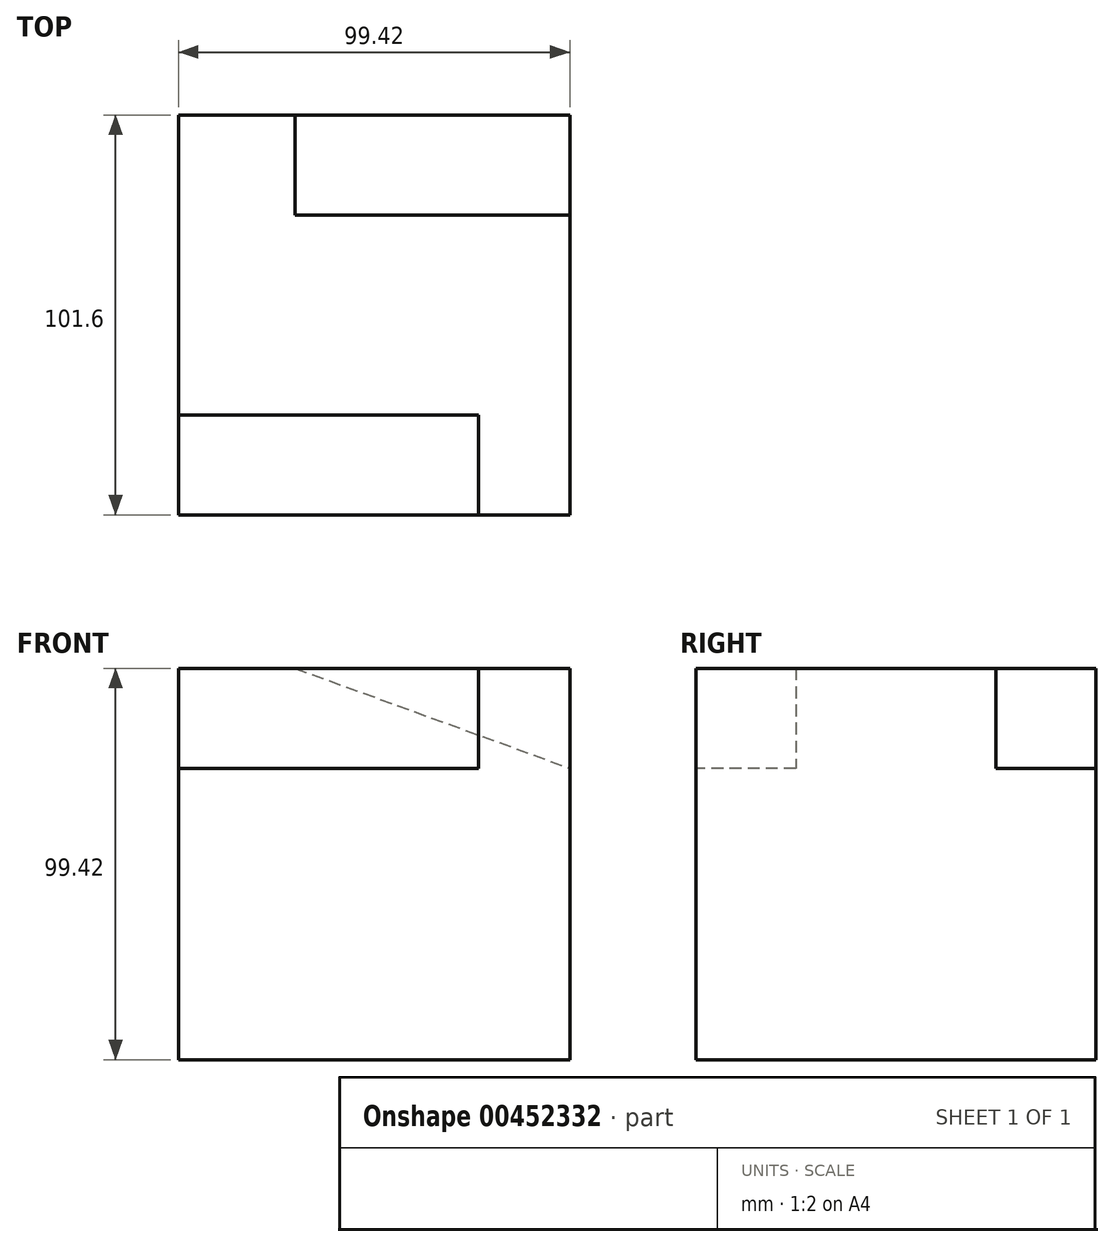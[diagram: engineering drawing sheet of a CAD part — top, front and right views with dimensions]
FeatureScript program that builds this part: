
annotation { "Feature Type Name" : "Feature", "Feature Type Description" : "" }
export const myFeature = defineFeature(function(context is Context, id is Id, definition is map)
    precondition{}
    {
        {
            var Q0;
            Q0=qCreatedBy(makeId("Front.planeOp"),FACE);
            var sketch = newSketch(context, id + "F0", { "sketchPlane" : qUnion([Q0])});
            skLineSegment(sketch, "E0.bottom", {"start": v(-49.71, 49.71) * mm, "end": v(49.71, 49.71) * mm});
            skLineSegment(sketch, "E0.top", {"start": v(-49.71, -49.71) * mm, "end": v(49.71, -49.71) * mm});
            skLineSegment(sketch, "E0.left", {"start": v(-49.71, 49.71) * mm, "end": v(-49.71, -49.71) * mm});
            skLineSegment(sketch, "E0.right", {"start": v(49.71, 49.71) * mm, "end": v(49.71, -49.71) * mm});
            skSolve(sketch);
        }
        {
            var Q0;
            Q0=makeQuery(id+"F0.imprint","IMPRINT",FACE,{"disambiguationData":[TD([[makeQuery(id+"F0.imprint","IMPRINT",EDGE,{"derivedFrom":sQuery(id+"F0.wireOp",EDGE,"E0.bottom")}),-1.0]])]});
            extrude(context, id + "F1", {"entities" : qUnion([Q0]), "endBound" : BoundingType.SYMMETRIC, "depth" : 101.6 * mm});
        }
        {
            var Q0;
            Q0=makeQuery(id+"F1.opExtrude","CAP_FACE",FACE,{"disambiguationData":[OSD([sQuery(id+"F0.wireOp",EDGE,"E0.bottom"),sQuery(id+"F0.wireOp",EDGE,"E0.top"),sQuery(id+"F0.wireOp",EDGE,"E0.left"),sQuery(id+"F0.wireOp",EDGE,"E0.right")])],"isStart":false});
            var sketch = newSketch(context, id + "F2", { "sketchPlane" : qUnion([Q0])});
            skLineSegment(sketch, "E1.bottom", {"start": v(-49.71, 49.71) * mm, "end": v(26.49, 49.71) * mm});
            skLineSegment(sketch, "E1.top", {"start": v(-49.71, 24.31) * mm, "end": v(26.49, 24.31) * mm});
            skLineSegment(sketch, "E1.left", {"start": v(-49.71, 49.71) * mm, "end": v(-49.71, 24.31) * mm});
            skLineSegment(sketch, "E1.right", {"start": v(26.49, 49.71) * mm, "end": v(26.49, 24.31) * mm});
            skSolve(sketch);
        }
        {
            var Q0;
            Q0=makeQuery(id+"F2.imprint","IMPRINT",FACE,{"disambiguationData":[TD([[makeQuery(id+"F2.imprint","IMPRINT",EDGE,{"derivedFrom":sQuery(id+"F2.wireOp",EDGE,"E1.bottom")}),-1.0]])]});
            extrude(context, id + "F3", {"entities" : qUnion([Q0]), "operationType" : NewBodyOperationType.REMOVE, "oppositeDirection" : true, "depth" : 25.4 * mm});
        }
        {
            var Q0;
            Q0=makeQuery(id+"F1.opExtrude","CAP_FACE",FACE,{"disambiguationData":[OSD([sQuery(id+"F0.wireOp",EDGE,"E0.bottom"),sQuery(id+"F0.wireOp",EDGE,"E0.top"),sQuery(id+"F0.wireOp",EDGE,"E0.left"),sQuery(id+"F0.wireOp",EDGE,"E0.right")])],"isStart":true});
            var sketch = newSketch(context, id + "F4", { "sketchPlane" : qUnion([Q0])});
            skLineSegment(sketch, "E2", {"start": v(20.07, 49.71) * mm, "end": v(-49.71, 24.31) * mm});
            skLineSegment(sketch, "E3", {"start": v(-49.71, 24.31) * mm, "end": v(-49.71, 49.71) * mm});
            skLineSegment(sketch, "E4", {"start": v(-49.71, 49.71) * mm, "end": v(20.07, 49.71) * mm});
            skSolve(sketch);
        }
        {
            var Q0;
            Q0 = qSketchRegion(id + "F4", true);
            extrude(context, id + "F5", {"entities" : qUnion([Q0]), "operationType" : NewBodyOperationType.REMOVE, "oppositeDirection" : true, "depth" : 25.4 * mm});
        }
        {
            var Q0;
            Q0=makeQuery(id+"F1.opExtrude","CAP_VERTEX",VERTEX,{"disambiguationData":[OSD([sQuery(id+"F0.wireOp",EDGE,"E0.bottom"),sQuery(id+"F0.wireOp",EDGE,"E0.right")])],"isStart":false});
            var Q1;
            Q1=makeQuery(id+"F1.opExtrude","CAP_VERTEX",VERTEX,{"disambiguationData":[OSD([sQuery(id+"F0.wireOp",EDGE,"E0.bottom"),sQuery(id+"F0.wireOp",EDGE,"E0.left")])],"isStart":true});
            var Q2;
            Q2=qCreatedBy(makeId("Origin.pointOp"),VERTEX);
            cPlane(context, id + "F6", {"entities" : qUnion([Q0, Q1, Q2]), "cplaneType" : CPlaneType.THREE_POINT, "offset" : 25.4 * mm, "width" : 152.4 * mm, "height" : 152.4 * mm});
        }
    });
